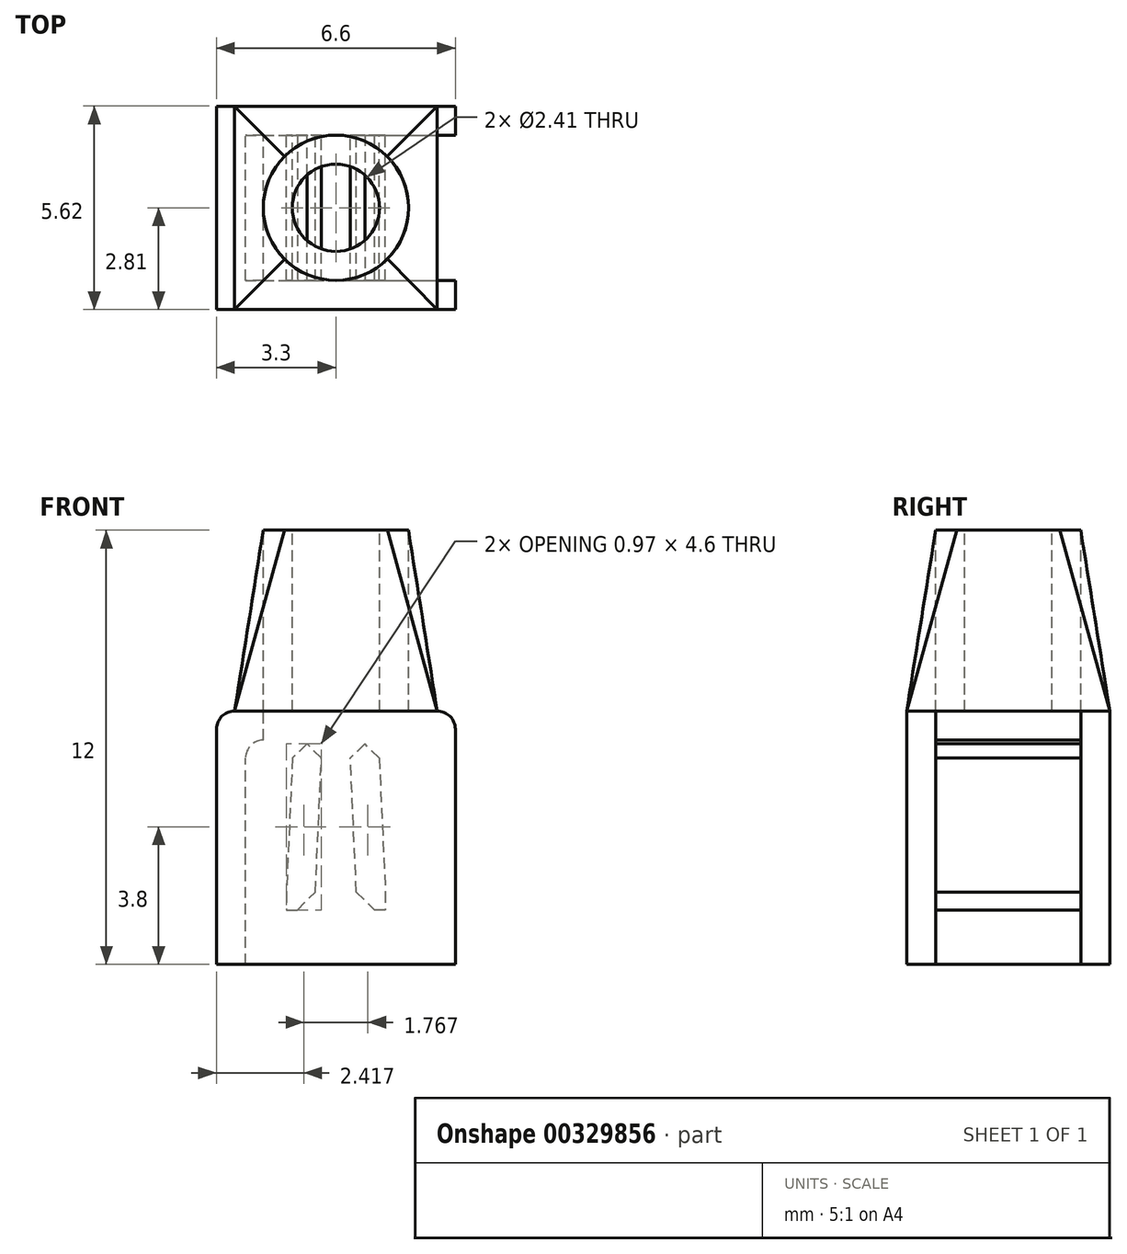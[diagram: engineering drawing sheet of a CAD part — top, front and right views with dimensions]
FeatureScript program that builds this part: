
annotation { "Feature Type Name" : "Feature", "Feature Type Description" : "" }
export const myFeature = defineFeature(function(context is Context, id is Id, definition is map)
    precondition{}
    {
        {
            var Q0;
            Q0=qCreatedBy(makeId("Front.planeOp"),FACE);
            var sketch = newSketch(context, id + "F0", { "sketchPlane" : qUnion([Q0])});
            skLineSegment(sketch, "E0", {"start": v(-1.2, 12) * mm, "end": v(-1.2, 7) * mm});
            skLineSegment(sketch, "E1", {"start": v(-1.2, 7) * mm, "end": v(-2, 7) * mm});
            skLineSegment(sketch, "E2", {"start": v(-2, 7) * mm, "end": v(-2, 12) * mm});
            skLineSegment(sketch, "E3", {"start": v(-2, 12) * mm, "end": v(-1.2, 12) * mm});
            skLineSegment(sketch, "E4", {"start": v(0, 12) * mm, "end": v(0, 7) * mm, "construction": true});
            skSolve(sketch);
        }
        {
            var Q0;
            Q0=makeQuery(id+"F0.imprint","IMPRINT",FACE,{"disambiguationData":[TD([[makeQuery(id+"F0.imprint","IMPRINT",EDGE,{"derivedFrom":sQuery(id+"F0.wireOp",EDGE,"E0")}),-1.0]])]});
            var Q1;
            Q1=sQuery(id+"F0.wireOp",EDGE,"E4");
            revolve(context, id + "F1", {"surfaceOperationType" : NewSurfaceOperationType.NEW, "entities" : qUnion([Q0]), "axis" : qUnion([Q1]), "revolveType" : RevolveType.FULL});
        }
        {
            var Q0;
            Q0=qCreatedBy(makeId("Front.planeOp"),FACE);
            var sketch = newSketch(context, id + "F2", { "sketchPlane" : qUnion([Q0])});
            skLineSegment(sketch, "E5", {"start": v(-3.3, 0) * mm, "end": v(-3.3, 6.5) * mm});
            skArc(sketch, "E6", {"start": v(-2.8, 7) * mm, "mid": v(-3.15, 6.85) * mm, "end": v(-3.3, 6.5) * mm});
            skLineSegment(sketch, "E7", {"start": v(-2.8, 7) * mm, "end": v(-2, 7) * mm});
            skLineSegment(sketch, "E8", {"start": v(-3.3, 0) * mm, "end": v(-2.5, 0) * mm});
            skLineSegment(sketch, "E9", {"start": v(-2.5, 0) * mm, "end": v(-2.5, 5.7) * mm});
            skArc(sketch, "E10", {"start": v(-2, 6.2) * mm, "mid": v(-2.35, 6.05) * mm, "end": v(-2.5, 5.7) * mm});
            skLineSegment(sketch, "E11", {"start": v(-2, 6.2) * mm, "end": v(-2, 6.2) * mm});
            skLineSegment(sketch, "E12", {"start": v(-2, 6.2) * mm, "end": v(-2, 7) * mm});
            skLineSegment(sketch, "E13", {"start": v(0, 0) * mm, "end": v(0, 7) * mm, "construction": true});
            skLineSegment(sketch, "E14", {"start": v(-1.2, 6.2) * mm, "end": v(-1.2, 5.7) * mm});
            skLineSegment(sketch, "E15", {"start": v(-1.2, 5.7) * mm, "end": v(-1.37, 2) * mm});
            skLineSegment(sketch, "E16", {"start": v(-1.37, 2) * mm, "end": v(-1.37, 1.5) * mm});
            skLineSegment(sketch, "E17", {"start": v(-1.37, 1.5) * mm, "end": v(-0.57, 1.5) * mm});
            skLineSegment(sketch, "E18", {"start": v(-0.57, 1.5) * mm, "end": v(-0.57, 2) * mm});
            skLineSegment(sketch, "E19", {"start": v(-0.57, 2) * mm, "end": v(-0.4, 5.7) * mm});
            skLineSegment(sketch, "E20", {"start": v(-0.4, 5.7) * mm, "end": v(-0.4, 6.2) * mm});
            skLineSegment(sketch, "E21", {"start": v(-0.4, 6.2) * mm, "end": v(-1.2, 6.2) * mm});
            skLineSegment(sketch, "E22", {"start": v(-1.2, 6.2) * mm, "end": v(-1.6, 6.2) * mm, "construction": true});
            skLineSegment(sketch, "E23", {"start": v(-1.6, 6.2) * mm, "end": v(-2, 6.2) * mm, "construction": true});
            skLineSegment(sketch, "E24", {"start": v(-0.4, 6.2) * mm, "end": v(0, 6.2) * mm, "construction": true});
            skLineSegment(sketch, "E25", {"start": v(-0.57, 1.5) * mm, "end": v(0, 1.5) * mm, "construction": true});
            skLineSegment(sketch, "E26", {"start": v(-1.37, 1.5) * mm, "end": v(-1.93, 1.5) * mm, "construction": true});
            skLineSegment(sketch, "E27", {"start": v(-1.93, 1.5) * mm, "end": v(-2.5, 1.5) * mm, "construction": true});
            skLineSegment(sketch, "E28.MirrorCS", {"start": v(0.4, 5.7) * mm, "end": v(0.4, 6.2) * mm});
            skLineSegment(sketch, "E29.MirrorCS", {"start": v(0.4, 6.2) * mm, "end": v(1.2, 6.2) * mm});
            skLineSegment(sketch, "E30.MirrorCS", {"start": v(1.2, 6.2) * mm, "end": v(1.2, 5.7) * mm});
            skLineSegment(sketch, "E31.MirrorCS", {"start": v(1.2, 5.7) * mm, "end": v(1.37, 2) * mm});
            skLineSegment(sketch, "E32.MirrorCS", {"start": v(0.57, 2) * mm, "end": v(0.4, 5.7) * mm});
            skLineSegment(sketch, "E33.MirrorCS", {"start": v(0.57, 1.5) * mm, "end": v(0.57, 2) * mm});
            skLineSegment(sketch, "E34.MirrorCS", {"start": v(1.37, 1.5) * mm, "end": v(0.57, 1.5) * mm});
            skLineSegment(sketch, "E35.MirrorCS", {"start": v(1.37, 2) * mm, "end": v(1.37, 1.5) * mm});
            skArc(sketch, "E36.MirrorCS", {"start": v(2, 6.2) * mm, "mid": v(2.35, 6.05) * mm, "end": v(2.5, 5.7) * mm});
            skLineSegment(sketch, "E37.MirrorCS", {"start": v(2, 6.2) * mm, "end": v(2, 7) * mm});
            skLineSegment(sketch, "E38.MirrorCS", {"start": v(2.8, 7) * mm, "end": v(2, 7) * mm});
            skArc(sketch, "E39.MirrorCS", {"start": v(2.8, 7) * mm, "mid": v(3.15, 6.85) * mm, "end": v(3.3, 6.5) * mm});
            skLineSegment(sketch, "E40.MirrorCS", {"start": v(3.3, 0) * mm, "end": v(3.3, 6.5) * mm});
            skLineSegment(sketch, "E41.MirrorCS", {"start": v(2.5, 0) * mm, "end": v(2.5, 5.7) * mm});
            skLineSegment(sketch, "E42.MirrorCS", {"start": v(3.3, 0) * mm, "end": v(2.5, 0) * mm});
            skSolve(sketch);
        }
        {
            var Q0;
            Q0 = qSketchRegion(id + "F2", true);
            extrude(context, id + "F3", {"entities" : qUnion([Q0]), "depth" : 2 * mm, "offsetDistance" : 25 * mm, "hasSecondDirection" : true, "secondDirectionOppositeDirection" : true, "secondDirectionDepth" : 2 * mm});
        }
        {
            var Q0;
            Q0=makeQuery(id+"F3.opExtrude","CAP_FACE",FACE,{"disambiguationData":[OSD([sQuery(id+"F2.wireOp",EDGE,"E5"),sQuery(id+"F2.wireOp",EDGE,"E6"),sQuery(id+"F2.wireOp",EDGE,"E7"),sQuery(id+"F2.wireOp",EDGE,"E8"),sQuery(id+"F2.wireOp",EDGE,"E9"),sQuery(id+"F2.wireOp",EDGE,"E10"),sQuery(id+"F2.wireOp",EDGE,"E12")])],"isStart":false});
            var sketch = newSketch(context, id + "F4", { "sketchPlane" : qUnion([Q0])});
            skLineSegment(sketch, "E43", {"start": v(-3.3, 0) * mm, "end": v(-3.3, 6.5) * mm});
            skArc(sketch, "E44", {"start": v(-2.8, 7) * mm, "mid": v(-3.15, 6.85) * mm, "end": v(-3.3, 6.5) * mm});
            skLineSegment(sketch, "E45", {"start": v(-2.8, 7) * mm, "end": v(2.8, 7) * mm});
            skArc(sketch, "E46", {"start": v(3.3, 6.5) * mm, "mid": v(3.15, 6.85) * mm, "end": v(2.8, 7) * mm});
            skLineSegment(sketch, "E47", {"start": v(3.3, 6.5) * mm, "end": v(3.3, 0) * mm});
            skLineSegment(sketch, "E48", {"start": v(3.3, 0) * mm, "end": v(-3.3, 0) * mm});
            skSolve(sketch);
        }
        {
            var Q0;
            Q0 = qSketchRegion(id + "F4", true);
            extrude(context, id + "F5", {"entities" : qUnion([Q0]), "depth" : 0.8 * mm, "offsetDistance" : 25 * mm});
        }
        {
            var Q0;
            Q0=makeQuery(id+"F5.opExtrude","SWEPT_BODY",BODY,{"disambiguationData":[OSD([sQuery(id+"F4.wireOp",EDGE,"E43"),sQuery(id+"F4.wireOp",EDGE,"E44"),sQuery(id+"F4.wireOp",EDGE,"E45"),sQuery(id+"F4.wireOp",EDGE,"E46"),sQuery(id+"F4.wireOp",EDGE,"E47"),sQuery(id+"F4.wireOp",EDGE,"E48")])]});
            var Q1;
            Q1=qCreatedBy(makeId("Front.planeOp"),FACE);
            mirror(context, id + "F6", {"operationType" : NewBodyOperationType.ADD, "entities" : qUnion([Q0]), "mirrorPlane" : qUnion([Q1])});
        }
        {
            var Q0;
            Q0=makeQuery(id+"F3.opExtrude","SWEPT_EDGE",EDGE,{"disambiguationData":[OSD([sQuery(id+"F2.wireOp",EDGE,"E29.MirrorCS"),sQuery(id+"F2.wireOp",EDGE,"E30.MirrorCS")])]});
            var Q1;
            Q1=makeQuery(id+"F3.opExtrude","SWEPT_EDGE",EDGE,{"disambiguationData":[OSD([sQuery(id+"F2.wireOp",EDGE,"E28.MirrorCS"),sQuery(id+"F2.wireOp",EDGE,"E29.MirrorCS")])]});
            var Q2;
            Q2=makeQuery(id+"F3.opExtrude","SWEPT_EDGE",EDGE,{"disambiguationData":[OSD([sQuery(id+"F2.wireOp",EDGE,"E20"),sQuery(id+"F2.wireOp",EDGE,"E21")])]});
            var Q3;
            Q3=makeQuery(id+"F3.opExtrude","SWEPT_EDGE",EDGE,{"disambiguationData":[OSD([sQuery(id+"F2.wireOp",EDGE,"E14"),sQuery(id+"F2.wireOp",EDGE,"E21")])]});
            var Q4;
            Q4=makeQuery(id+"F3.opExtrude","SWEPT_EDGE",EDGE,{"disambiguationData":[OSD([sQuery(id+"F2.wireOp",EDGE,"E33.MirrorCS"),sQuery(id+"F2.wireOp",EDGE,"E34.MirrorCS")])]});
            var Q5;
            Q5=makeQuery(id+"F3.opExtrude","SWEPT_EDGE",EDGE,{"disambiguationData":[OSD([sQuery(id+"F2.wireOp",EDGE,"E17"),sQuery(id+"F2.wireOp",EDGE,"E18")])]});
            chamfer(context, id + "F7", {"entities" : qUnion([Q0, Q1, Q2, Q3, Q4, Q5]), "width" : 0.5 * mm, "tangentPropagation" : true});
        }
        {
            var Q0;
            {var subQ0=makeQuery(id+"F5.opExtrude","SWEPT_FACE",FACE,{"disambiguationData":[OSD([sQuery(id+"F4.wireOp",EDGE,"E45")])]});Q0=makeQuery(id+"F6.boolean.opBoolean","MERGE",FACE,{"derivedFrom":[makeQuery(id+"F3.opExtrude","SWEPT_FACE",FACE,{"disambiguationData":[OSD([sQuery(id+"F2.wireOp",EDGE,"E7")])]}),makeQuery(id+"F3.opExtrude","SWEPT_FACE",FACE,{"disambiguationData":[OSD([sQuery(id+"F2.wireOp",EDGE,"E38.MirrorCS")])]}),subQ0,makeQuery(id+"F6.opPattern","COPY",FACE,{"derivedFrom":subQ0,"instanceName":"1"})]});}
            var sketch = newSketch(context, id + "F8", { "sketchPlane" : qUnion([Q0])});
            skLineSegment(sketch, "E49.bottom", {"start": v(-2.8, 2.8) * mm, "end": v(2.8, 2.8) * mm});
            skLineSegment(sketch, "E49.top", {"start": v(-2.8, -2.8) * mm, "end": v(2.8, -2.8) * mm});
            skLineSegment(sketch, "E49.left", {"start": v(-2.8, 2.8) * mm, "end": v(-2.8, -2.8) * mm});
            skLineSegment(sketch, "E49.right", {"start": v(2.8, 2.8) * mm, "end": v(2.8, -2.8) * mm});
            skSolve(sketch);
        }
        {
            var Q0;
            Q0=makeQuery(id+"F1.opRevolve","SWEPT_FACE",FACE,{"disambiguationData":[OSD([sQuery(id+"F0.wireOp",EDGE,"E3")])]});
            var sketch = newSketch(context, id + "F9", { "sketchPlane" : qUnion([Q0])});
            skCircle(sketch, "E50", {"center": v(0, 0) * mm, "radius": 2 * mm});
            skSolve(sketch);
        }
        {
            var Q0;
            Q0 = qSketchRegion(id + "F8", true);
            var Q1;
            Q1 = qSketchRegion(id + "F9", true);
            loft(context, id + "F10", {"sheetProfilesArray" : [{ "sheetProfileEntities" : qUnion([Q0]) }, { "sheetProfileEntities" : qUnion([Q1]) }]});
        }
        {
            var Q0;
            Q0=makeQuery(id+"F9.imprint","IMPRINT",FACE,{"disambiguationData":[TD([[makeQuery(id+"F9.imprint","IMPRINT",EDGE,{"derivedFrom":sQuery(id+"F9.wireOp",EDGE,"E50")}),1.0]])]});
            var sketch = newSketch(context, id + "F11", { "sketchPlane" : qUnion([Q0])});
            skCircle(sketch, "E51", {"center": v(0, 0) * mm, "radius": 1.2 * mm});
            skSolve(sketch);
        }
        {
            var Q0;
            Q0 = qSketchRegion(id + "F11", true);
            var Q1;
            Q1=makeQuery(id+"F1.opRevolve","SWEPT_FACE",FACE,{"disambiguationData":[OSD([sQuery(id+"F0.wireOp",EDGE,"E1")])]});
            extrude(context, id + "F12", {"entities" : qUnion([Q0]), "operationType" : NewBodyOperationType.REMOVE, "endBound" : BoundingType.UP_TO_SURFACE, "oppositeDirection" : true, "depth" : 25 * mm, "endBoundEntityFace" : qUnion([Q1]), "offsetDistance" : 25 * mm});
        }
    });
